# Revit family: PRD_FrankeWS_WtrSpplFttngsFrWshBsnsAndTrghs_SelfClosingPillarMixer_F5SV1001,1002
name_source: partatom
category: Plumbing Fixtures
revit_build: Autodesk Revit 2018 (Build: 20190510_1515(x64)
units: mm (PartAtom-declared; Revit-internal decimal feet)

## family parameters
Always vertical = Yes
Cut with Voids When Loaded = No
OmniClass Number = 23.45.55.14
OmniClass Title = Single Faucets
Part Type = Normal
Room Calculation Point = No
Round Connector Dimension = Use Diameter
Shared = No
Work Plane-Based = Yes

## types (2) — shared parameters
AdjustableFlowTime = yes
AssetType = Fixed
Category = Pr_40_20_87_98, Washbasin taps
Color = Chrome
Default Elevation = 750 mm  [stored 2.46063 ft]
Depressurised = no
DiameterNominal = 15 mm
DurationUnit = year
FaucetFunction = MIXED
FaucetMaterial = PRD_AR_ChromatedBrass_HighPolished
FaucetOperation = SELFCLOSING
FaucetType = PILLAR
Finish = high-polished chromium-plated brass
FlowColdWater = 0.2 L/s
Form = Self-closing
FunctionalPrinciple = Hydraulic self-closing
GrossWeight = 1.72 kg
HygieneFlushing = no
IfcExportAs = IfcValveType
IfcExportType = FAUCET
InletSize = DN 15 (3/8 inch.)
Manufacturer = KWC Group AG
ManufacturerName = KWC Group AG
ManufacturerURL = www.kwc.com
Material = Brass
MaximumFlowTime = 35.00 seconds
MinimumFlowPressure = 0.50 bar
MinimumFlowTime = 5.00 seconds
NBSDescription = Water supply fittings for wash basins and troughs
NBSReference = 45-35-70/371
NetWeight = 1.60 kg
OutletMaterial = PRD_AR_SyntheticGrey
ProductInformation = https://pim.kwc.com
ProtectiveShutdown = no
SoundInsulation = no
SpoutProjection = 125.00 mm
ThermalDisinfection = no
TypeOfMixing = no mixing
TypeOfMounting = TAPHOLE
TypeOfOperation = Manual operation
TypeOfTap = pillar tap
URL = www.kwc.com
Uniclass2015Code = Pr_40_20_87_98
Uniclass2015Title = Washbasin taps
Uniclass2015Version = Products v1.10
Version = 1
WarrantyDurationUnit = year
zero-valued in all types: NominalDepth, NominalHeight, NominalWidth

## per-type parameters (varying)
| type | BIMObjectName | Description | Model | ModelNumber | ModelReference | Name | VolumeFlowRate |
| F5SV1001 - 0.08 L/s | PRD_AR_WaterSupplyFittingsForWashBasinsAndTroughs_SelfClosingPillarTap_F5SV1001 | F5S self-closing pillar tap DN 15 for sanitary facilities. FRAMIC self-closing cartridge, hydraulically controlled, low-maintenance and stagnation-free, with ceramic disc technology, self-closing, flow pressure-independent due to medium-separated design. Stepless adjustment of flow duration. For connection to pre-mixed hot water or cold water via hose including strainer seal. All-metal construction, high-polished chromium-plated brass. Anti-theft aerator, SLIM design, with integrated flow regulator 5.0 l/min. | F5SV1001 | 2030036165 | F5SV1001 | F5 self-closing pillar tap F5SV1001 | 0.08 L/s at 3 bar |
| F5SV1002 - 0.05 L/s | PRD_AR_WaterSupplyFittingsForWashBasinsAndTroughs_SelfClosingPillarTap_F5SV1002 | F5S self-closing pillar tap DN 15 for sanitary facilities. FRAMIC self-closing cartridge, hydraulically controlled, low-maintenance and stagnation-free, with ceramic disc technology, self-closing, flow pressure-independent due to medium-separated design. Stepless adjustment of flow duration. For connection to pre-mixed hot water or cold water via hose including strainer seal. All-metal construction, high-polished chromium-plated brass. Aerator with integrated flow regulator 3.0 l/min. | F5SV1002 | 2030039426 | F5SV1002 | F5 self-closing pillar tap F5SV1002 | 0.05 L/s at 3 bar |

note: [stored X ft] marks values corroborated as IEEE doubles in the binary element streams (Revit-internal decimal feet)

## geometry (parser evidence)
native form markers: Sweep x2
no freeform markers — native parametric forms only
